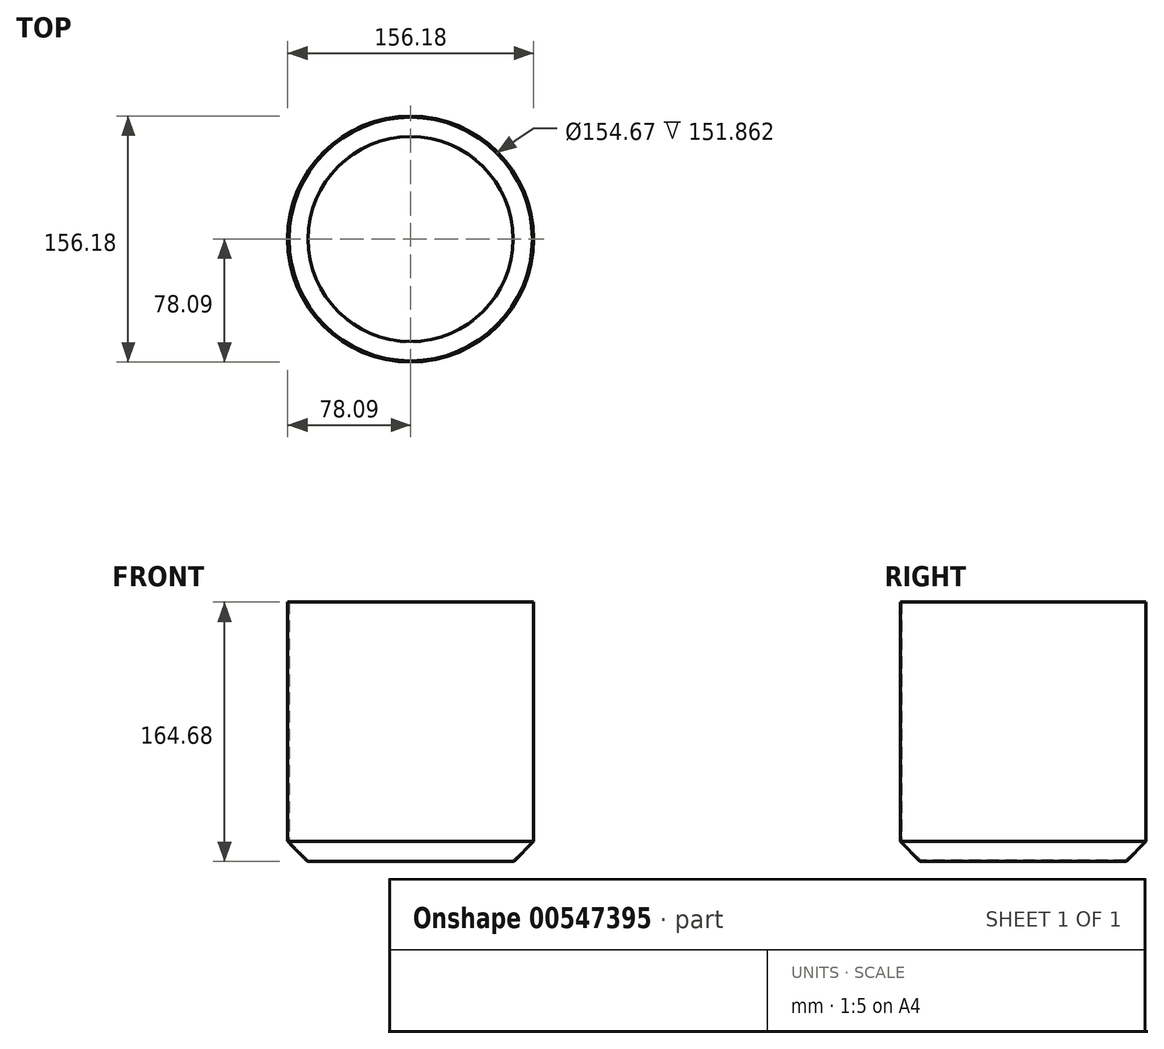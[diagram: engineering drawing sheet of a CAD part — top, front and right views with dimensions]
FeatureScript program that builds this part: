
annotation { "Feature Type Name" : "Feature", "Feature Type Description" : "" }
export const myFeature = defineFeature(function(context is Context, id is Id, definition is map)
    precondition{}
    {
        {
            var Q0;
            Q0=qCreatedBy(makeId("Front.planeOp"),FACE);
            var sketch = newSketch(context, id + "F0", { "sketchPlane" : qUnion([Q0])});
            skLineSegment(sketch, "E0", {"start": v(-77.33, 12.28) * mm, "end": v(-65.05, 0) * mm});
            skLineSegment(sketch, "E1", {"start": v(-77.33, 12.28) * mm, "end": v(-77.33, 164.14) * mm});
            skLineSegment(sketch, "E2", {"start": v(-77.33, 164.14) * mm, "end": v(-78.1, 164.14) * mm});
            skLineSegment(sketch, "E3", {"start": v(-77.33, 12.28) * mm, "end": v(-78.1, 12.28) * mm});
            skLineSegment(sketch, "E4", {"start": v(-78.1, 164.14) * mm, "end": v(-78.1, 12.28) * mm});
            skLineSegment(sketch, "E5", {"start": v(-65.05, 0) * mm, "end": v(-65.59, -0.54) * mm});
            skLineSegment(sketch, "E6", {"start": v(-78.1, 12.28) * mm, "end": v(-65.59, -0.54) * mm});
            skSolve(sketch);
        }
        {
            var Q0;
            Q0=qCreatedBy(makeId("Front.planeOp"),FACE);
            var sketch = newSketch(context, id + "F1", { "sketchPlane" : qUnion([Q0])});
            skLineSegment(sketch, "E7", {"start": v(0, 33.16) * mm, "end": v(0, 58.38) * mm});
            skSolve(sketch);
        }
        {
            var Q0;
            Q0 = qSketchRegion(id + "F0", true);
            var Q1;
            Q1=sQuery(id+"F1.wireOp",EDGE,"E7");
            revolve(context, id + "F2", {"entities" : qUnion([Q0]), "axis" : qUnion([Q1]), "revolveType" : RevolveType.FULL});
        }
    });
